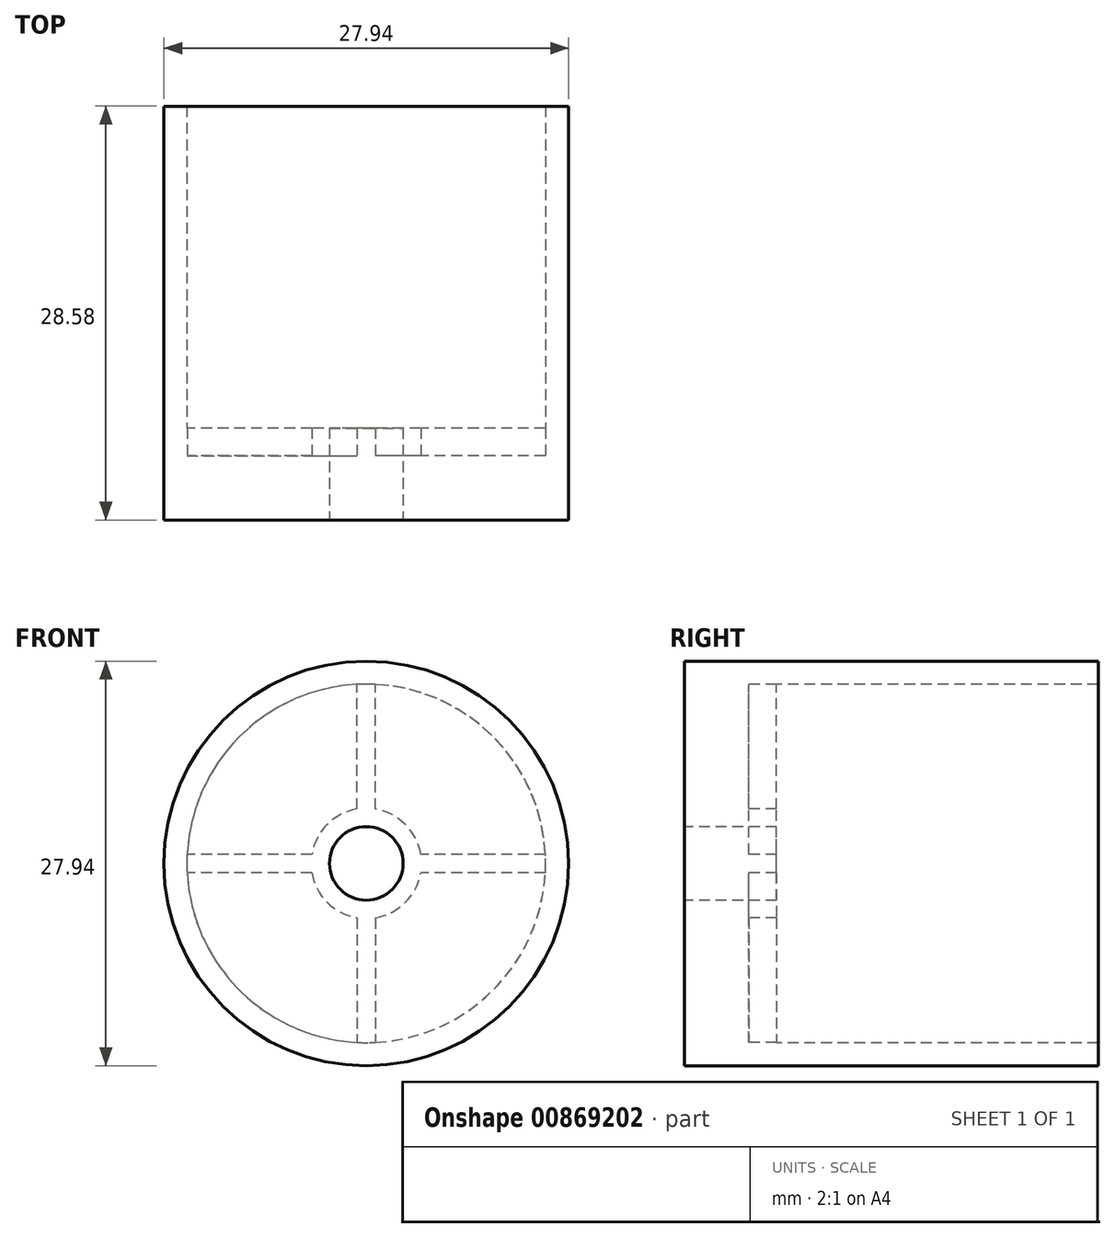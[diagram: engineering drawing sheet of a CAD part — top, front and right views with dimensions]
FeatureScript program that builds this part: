
annotation { "Feature Type Name" : "Feature", "Feature Type Description" : "" }
export const myFeature = defineFeature(function(context is Context, id is Id, definition is map)
    precondition{}
    {
        {
            var Q0;
            Q0=qCreatedBy(makeId("Front.planeOp"),FACE);
            var sketch = newSketch(context, id + "F0", { "sketchPlane" : qUnion([Q0])});
            skCircle(sketch, "E0", {"center": v(0, 0) * mm, "radius": 13.97 * mm});
            skCircle(sketch, "E1", {"center": v(0, 0) * mm, "radius": 2.54 * mm});
            skSolve(sketch);
        }
        {
            var Q0;
            Q0 = qSketchRegion(id + "F0", true);
            extrude(context, id + "F1", {"entities" : qUnion([Q0]), "oppositeDirection" : true, "depth" : 4.44 * mm, "offsetDistance" : 25.4 * mm});
        }
        {
            var Q0;
            Q0=makeQuery(id+"F1.opExtrude","CAP_FACE",FACE,{"disambiguationData":[OSD([sQuery(id+"F0.wireOp",EDGE,"E0"),sQuery(id+"F0.wireOp",EDGE,"E1")])],"isStart":false});
            var sketch = newSketch(context, id + "F2", { "sketchPlane" : qUnion([Q0])});
            skCircle(sketch, "E2", {"center": v(0, 0) * mm, "radius": 13.97 * mm});
            skCircle(sketch, "E3", {"center": v(0, 0) * mm, "radius": 12.38 * mm});
            skSolve(sketch);
        }
        {
            var Q0;
            Q0 = qSketchRegion(id + "F2", true);
            extrude(context, id + "F3", {"entities" : qUnion([Q0]), "operationType" : NewBodyOperationType.ADD, "depth" : 24.13 * mm, "offsetDistance" : 25.4 * mm});
        }
        {
            var Q0;
            Q0=makeQuery(id+"F1.opExtrude","CAP_FACE",FACE,{"disambiguationData":[OSD([sQuery(id+"F0.wireOp",EDGE,"E0"),sQuery(id+"F0.wireOp",EDGE,"E1")])],"isStart":false});
            var sketch = newSketch(context, id + "F4", { "sketchPlane" : qUnion([Q0])});
            skCircle(sketch, "E4", {"center": v(0, 0) * mm, "radius": 2.54 * mm});
            skArc(sketch, "E5.0", {"start": v(-3.76, -0.63) * mm, "mid": v(-2.7, -2.7) * mm, "end": v(-0.64, -3.76) * mm});
            skLineSegment(sketch, "E6.0", {"start": v(-12.5, -0.63) * mm, "end": v(-3.76, -0.63) * mm});
            skLineSegment(sketch, "E7.0", {"start": v(-0.64, -3.76) * mm, "end": v(-0.63, -12.38) * mm});
            skLineSegment(sketch, "E8.0", {"start": v(0.63, -3.76) * mm, "end": v(0.64, -12.38) * mm});
            skLineSegment(sketch, "E9", {"start": v(-0.63, -12.38) * mm, "end": v(0.64, -12.38) * mm});
            skLineSegment(sketch, "E10.MirrorCS", {"start": v(-12.5, 0.63) * mm, "end": v(-3.76, 0.63) * mm});
            skLineSegment(sketch, "E11.MirrorCS", {"start": v(-0.64, 3.76) * mm, "end": v(-0.63, 12.38) * mm});
            skLineSegment(sketch, "E12.MirrorCS", {"start": v(0.63, 3.76) * mm, "end": v(0.64, 12.38) * mm});
            skLineSegment(sketch, "E13", {"start": v(-0.63, 12.38) * mm, "end": v(0.64, 12.38) * mm});
            skLineSegment(sketch, "E14", {"start": v(12.38, 0.63) * mm, "end": v(12.38, -0.63) * mm});
            skLineSegment(sketch, "E15", {"start": v(-12.5, 0.63) * mm, "end": v(-12.5, -0.63) * mm});
            skLineSegment(sketch, "E16.trimOffspring", {"start": v(3.76, -0.63) * mm, "end": v(12.38, -0.63) * mm});
            skLineSegment(sketch, "E17.trimOffspring", {"start": v(3.76, 0.63) * mm, "end": v(12.38, 0.63) * mm});
            skArc(sketch, "E18.trimOffspring", {"start": v(0.63, -3.76) * mm, "mid": v(2.7, -2.7) * mm, "end": v(3.76, -0.63) * mm});
            skArc(sketch, "E19.trimOffspring", {"start": v(3.76, 0.64) * mm, "mid": v(2.7, 2.7) * mm, "end": v(0.63, 3.76) * mm});
            skArc(sketch, "E20.trimOffspring", {"start": v(-0.64, 3.76) * mm, "mid": v(-2.7, 2.7) * mm, "end": v(-3.76, 0.63) * mm});
            skSolve(sketch);
        }
        {
            var Q0;
            Q0 = qSketchRegion(id + "F4", true);
            extrude(context, id + "F5", {"entities" : qUnion([Q0]), "operationType" : NewBodyOperationType.ADD, "depth" : 1.9 * mm, "offsetDistance" : 25.4 * mm});
        }
    });
